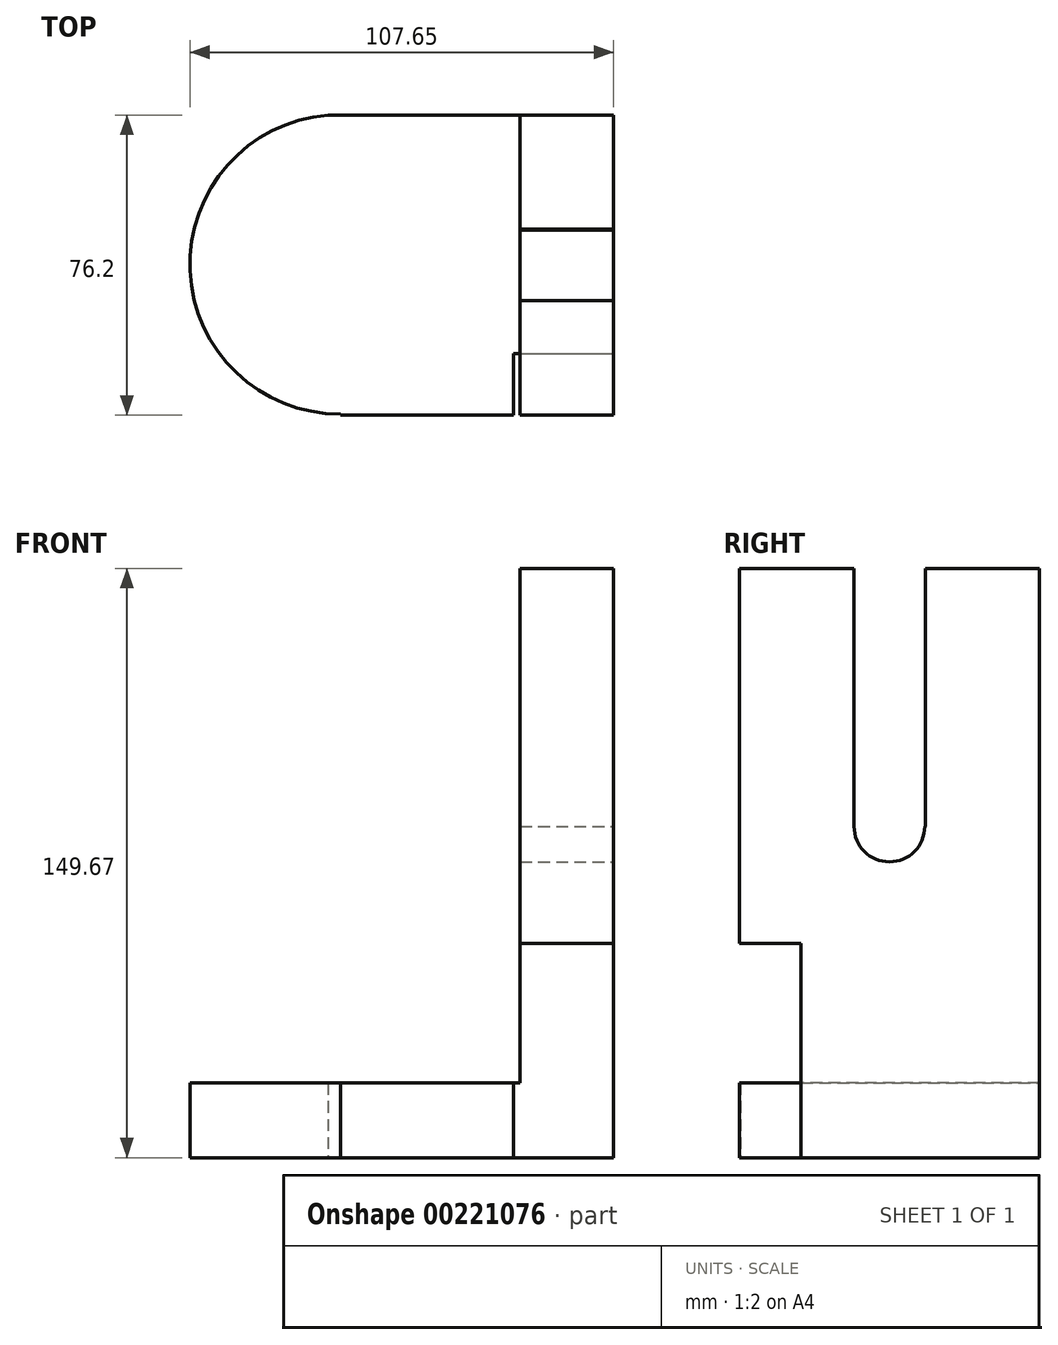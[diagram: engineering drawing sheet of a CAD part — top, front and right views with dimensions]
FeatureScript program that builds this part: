
annotation { "Feature Type Name" : "Feature", "Feature Type Description" : "" }
export const myFeature = defineFeature(function(context is Context, id is Id, definition is map)
    precondition{}
    {
        {
            var Q0;
            Q0=qCreatedBy(makeId("Front.planeOp"),FACE);
            var sketch = newSketch(context, id + "F0", { "sketchPlane" : qUnion([Q0])});
            skLineSegment(sketch, "E0.bottom", {"start": v(31.43, 74.45) * mm, "end": v(55.2, 74.45) * mm});
            skLineSegment(sketch, "E0.top", {"start": v(-52.5, -75.22) * mm, "end": v(55.2, -75.22) * mm});
            skLineSegment(sketch, "E0.left", {"start": v(-52.5, -56.25) * mm, "end": v(-52.5, -75.22) * mm});
            skLineSegment(sketch, "E0.right", {"start": v(55.2, 74.45) * mm, "end": v(55.2, -75.22) * mm});
            skLineSegment(sketch, "E1.top", {"start": v(-52.5, -56.25) * mm, "end": v(31.43, -56.25) * mm});
            skLineSegment(sketch, "E1.right", {"start": v(31.43, 74.45) * mm, "end": v(31.43, -56.25) * mm});
            skSolve(sketch);
        }
        {
            var Q0;
            Q0=makeQuery(id+"F0.imprint","IMPRINT",FACE,{"disambiguationData":[TD([[makeQuery(id+"F0.imprint","IMPRINT",EDGE,{"derivedFrom":sQuery(id+"F0.wireOp",EDGE,"E0.bottom")}),-1.0]])]});
            extrude(context, id + "F1", {"entities" : qUnion([Q0]), "depth" : 76.2 * mm});
        }
        {
            var Q0;
            Q0=makeQuery(id+"F1.opExtrude","SWEPT_FACE",FACE,{"disambiguationData":[OSD([sQuery(id+"F0.wireOp",EDGE,"E0.right")])]});
            var sketch = newSketch(context, id + "F2", { "sketchPlane" : qUnion([Q0])});
            skCircle(sketch, "E2", {"center": v(-38.14, 8.91) * mm, "radius": 8.98 * mm});
            skLineSegment(sketch, "E3.bottom", {"start": v(-47.12, 8.91) * mm, "end": v(-28.94, 8.91) * mm});
            skLineSegment(sketch, "E3.top", {"start": v(-47.12, 74.45) * mm, "end": v(-28.94, 74.45) * mm});
            skLineSegment(sketch, "E3.left", {"start": v(-47.12, 8.91) * mm, "end": v(-47.12, 74.45) * mm});
            skLineSegment(sketch, "E3.right", {"start": v(-28.94, 8.91) * mm, "end": v(-28.94, 74.45) * mm});
            skSolve(sketch);
        }
        {
            var Q0;
            {var subQ0=sQuery(id+"F2.wireOp",EDGE,"E3.bottom");var subQ1=sQuery(id+"F2.wireOp",EDGE,"E2");var subQ3=makeQuery(id+"F2.imprint","INTERSECT",VERTEX,{"derivedFrom":[subQ1,subQ0]});Q0=makeQuery(id+"F2.imprint","IMPRINT",FACE,{"disambiguationData":[TD([[makeQuery(id+"F2.imprint","IMPRINT",EDGE,{"disambiguationData":[TD([[subQ3,1.0]])],"derivedFrom":subQ1}),1.0]])]});}
            var Q1;
            Q1=makeQuery(id+"F2.imprint","IMPRINT",FACE,{"disambiguationData":[TD([[makeQuery(id+"F2.imprint","IMPRINT",EDGE,{"derivedFrom":sQuery(id+"F2.wireOp",EDGE,"E3.top")}),-1.0]])]});
            extrude(context, id + "F3", {"entities" : qUnion([Q0, Q1]), "operationType" : NewBodyOperationType.REMOVE, "endBound" : BoundingType.THROUGH_ALL, "oppositeDirection" : true, "depth" : 25.4 * mm});
        }
        {
            var Q0;
            {var subQ0=sQuery(id+"F2.wireOp",EDGE,"E3.bottom");var subQ1=sQuery(id+"F2.wireOp",EDGE,"E2");var subQ3=makeQuery(id+"F2.imprint","INTERSECT",VERTEX,{"derivedFrom":[subQ1,subQ0]});Q0=makeQuery(id+"F3.boolean.opBoolean","SPLIT",FACE,{"disambiguationData":[TD([makeQuery(id+"F3.opExtrude","SWEPT_FACE",FACE,{"disambiguationData":[OSD([subQ1]),TDD([makeQuery(id+"F2.imprint","IMPRINT",EDGE,{"disambiguationData":[TD([[subQ3,-1.0]])],"derivedFrom":subQ1})])]})])],"derivedFrom":makeQuery(id+"F1.opExtrude","SWEPT_FACE",FACE,{"disambiguationData":[OSD([sQuery(id+"F0.wireOp",EDGE,"E0.right")])]})});}
            extrude(context, id + "F4", {"entities" : qUnion([Q0]), "operationType" : NewBodyOperationType.REMOVE, "endBound" : BoundingType.THROUGH_ALL, "oppositeDirection" : true, "depth" : 25.4 * mm});
        }
        {
            var Q0;
            {var subQ4=sQuery(id+"F0.wireOp",EDGE,"E0.right");var subQ6=sQuery(id+"F0.wireOp",EDGE,"E0.bottom");Q0=makeQuery(id+"F3.boolean.opBoolean","SPLIT",FACE,{"disambiguationData":[TD([makeQuery(id+"F1.opExtrude","SWEPT_FACE",FACE,{"disambiguationData":[OSD([subQ6])]})])],"derivedFrom":makeQuery(id+"F1.opExtrude","SWEPT_FACE",FACE,{"disambiguationData":[OSD([subQ4])]})});}
            var sketch = newSketch(context, id + "F5", { "sketchPlane" : qUnion([Q0])});
            skLineSegment(sketch, "E4.bottom", {"start": v(-76.2, -20.8) * mm, "end": v(-60.56, -20.8) * mm});
            skLineSegment(sketch, "E4.top", {"start": v(-76.2, -75.22) * mm, "end": v(-60.56, -75.22) * mm});
            skLineSegment(sketch, "E4.left", {"start": v(-76.2, -20.8) * mm, "end": v(-76.2, -75.22) * mm});
            skLineSegment(sketch, "E4.right", {"start": v(-60.56, -20.8) * mm, "end": v(-60.56, -75.22) * mm});
            skSolve(sketch);
        }
        {
            var Q0;
            Q0=makeQuery(id+"F5.imprint","IMPRINT",FACE,{"disambiguationData":[TD([[makeQuery(id+"F5.imprint","IMPRINT",EDGE,{"derivedFrom":sQuery(id+"F5.wireOp",EDGE,"E4.bottom")}),-1.0]])]});
            extrude(context, id + "F6", {"entities" : qUnion([Q0]), "operationType" : NewBodyOperationType.REMOVE, "oppositeDirection" : true, "depth" : 25.4 * mm});
        }
        {
            var Q0;
            Q0=makeQuery(id+"F1.opExtrude","SWEPT_FACE",FACE,{"disambiguationData":[OSD([sQuery(id+"F0.wireOp",EDGE,"E0.top")])]});
            var sketch = newSketch(context, id + "F7", { "sketchPlane" : qUnion([Q0])});
            skArc(sketch, "E5", {"start": v(-14.16, 75.92) * mm, "mid": v(-52.46, 37.92) * mm, "end": v(-14.18, -0.11) * mm});
            skLineSegment(sketch, "E6", {"start": v(-14.16, 75.92) * mm, "end": v(-14.16, 85) * mm});
            skLineSegment(sketch, "E7", {"start": v(-14.37, 85) * mm, "end": v(-71.67, 85) * mm});
            skLineSegment(sketch, "E8", {"start": v(-71.67, 85) * mm, "end": v(-69.95, -10.44) * mm});
            skLineSegment(sketch, "E9", {"start": v(-69.95, -10.44) * mm, "end": v(-14.16, -10.44) * mm});
            skLineSegment(sketch, "E10", {"start": v(-14.18, -11.6) * mm, "end": v(-14.18, -0.11) * mm});
            skSolve(sketch);
        }
        {
            var Q0;
            {var subQ0=sQuery(id+"F0.wireOp",EDGE,"E0.top");var subQ2=makeQuery(id+"F1.opExtrude","SWEPT_EDGE",EDGE,{"disambiguationData":[OSD([subQ0,sQuery(id+"F0.wireOp",EDGE,"E0.left")])]});Q0=makeQuery(id+"F7.imprint","IMPRINT",FACE,{"disambiguationData":[TD([[makeQuery(id+"F7.imprint","IMPRINT",EDGE,{"derivedFrom":subQ2}),1.0]])]});}
            extrude(context, id + "F8", {"entities" : qUnion([Q0]), "operationType" : NewBodyOperationType.REMOVE, "endBound" : BoundingType.THROUGH_ALL, "oppositeDirection" : true, "depth" : 25.4 * mm});
        }
    });
